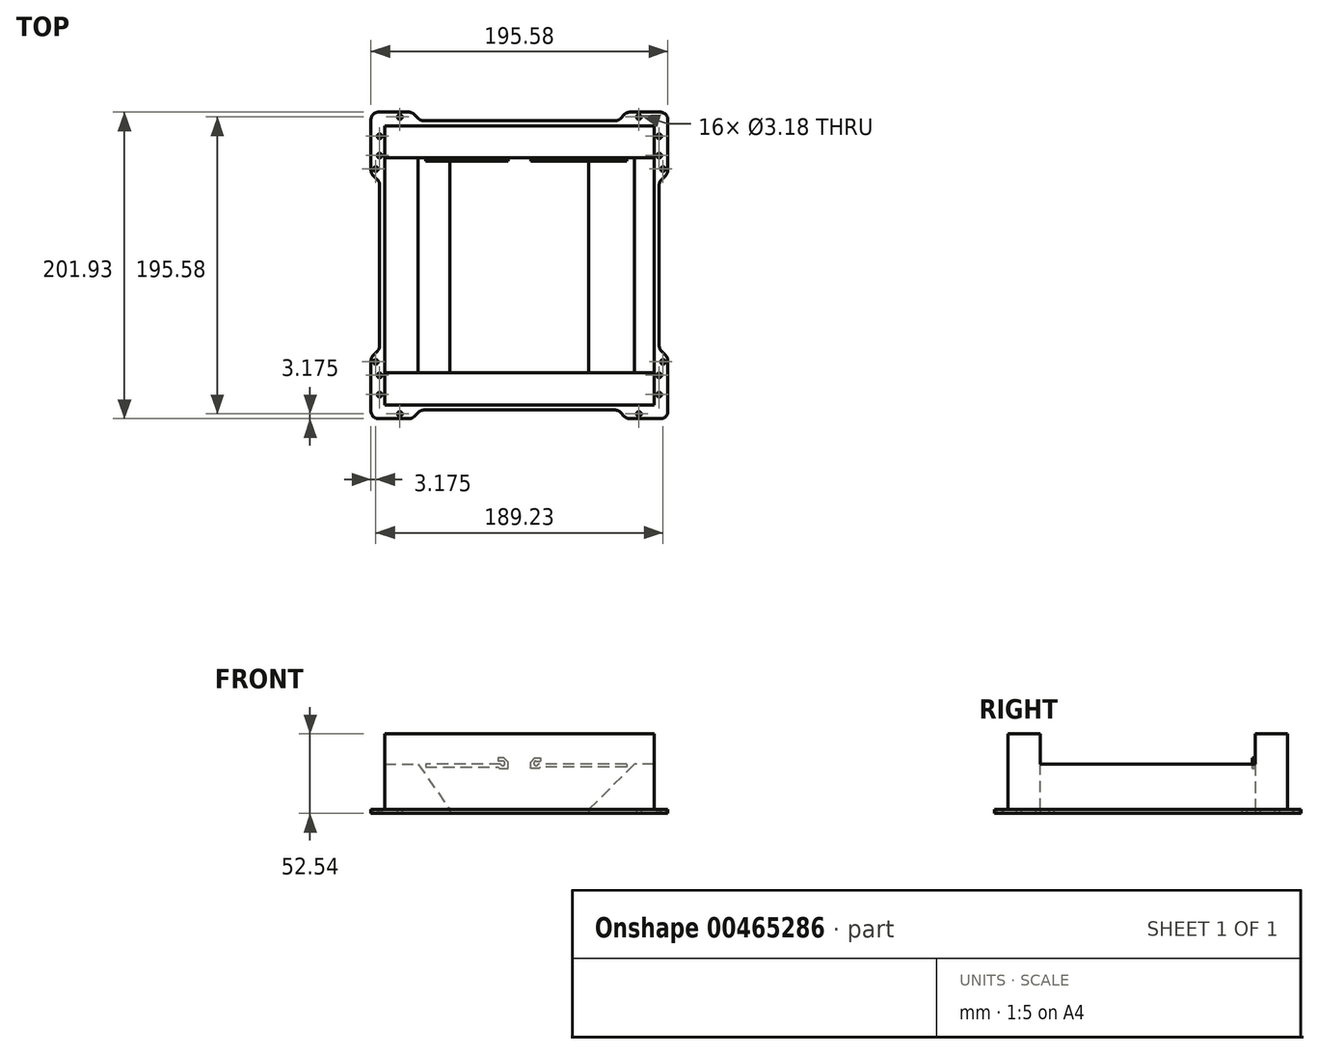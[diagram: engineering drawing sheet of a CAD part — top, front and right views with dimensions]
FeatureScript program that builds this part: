
annotation { "Feature Type Name" : "Feature", "Feature Type Description" : "" }
export const myFeature = defineFeature(function(context is Context, id is Id, definition is map)
    precondition{}
    {
        {
            var Q0;
            Q0=qCreatedBy(makeId("Top.planeOp"),FACE);
            var sketch = newSketch(context, id + "F0", { "sketchPlane" : qUnion([Q0])});
            skLineSegment(sketch, "E0.bottom", {"start": v(5, 0) * mm, "end": v(25, 0) * mm});
            skLineSegment(sketch, "E0.top", {"start": v(5, 201.93) * mm, "end": v(25, 201.93) * mm});
            skLineSegment(sketch, "E0.left", {"start": v(0, 5) * mm, "end": v(0, 38.18) * mm});
            skLineSegment(sketch, "E0.right", {"start": v(195.58, 5) * mm, "end": v(195.58, 38.18) * mm});
            skLineSegment(sketch, "E1.bottom", {"start": v(52.07, 171.77) * mm, "end": v(143.5, 171.77) * mm});
            skLineSegment(sketch, "E1.top", {"start": v(52.07, 30.17) * mm, "end": v(143.5, 30.17) * mm});
            skLineSegment(sketch, "E1.left", {"start": v(52.07, 171.77) * mm, "end": v(52.07, 30.17) * mm});
            skLineSegment(sketch, "E1.right", {"start": v(143.5, 171.77) * mm, "end": v(143.5, 30.17) * mm});
            skLineSegment(sketch, "E2", {"start": v(97.79, 232) * mm, "end": v(97.79, -11.17) * mm, "construction": true});
            skPoint(sketch, "E2.startSnap0", {"position": v(97.79, 201.93) * mm});
            skLineSegment(sketch, "E3", {"start": v(-12.15, 100.97) * mm, "end": v(206.64, 100.97) * mm, "construction": true});
            skPoint(sketch, "E3.startSnap0", {"position": v(0, 100.97) * mm});
            skPoint(sketch, "E4.visualSharp", {"position": v(0, 201.93) * mm});
            skArc(sketch, "E4.filletArc", {"start": v(5, 201.93) * mm, "mid": v(1.46, 200.47) * mm, "end": v(0, 196.93) * mm});
            skPoint(sketch, "E5.visualSharp", {"position": v(195.58, 201.93) * mm});
            skArc(sketch, "E5.filletArc", {"start": v(195.58, 196.93) * mm, "mid": v(194.12, 200.47) * mm, "end": v(190.58, 201.93) * mm});
            skArc(sketch, "E6.filletArc", {"start": v(0, 5) * mm, "mid": v(1.46, 1.46) * mm, "end": v(5, 0) * mm});
            skPoint(sketch, "E7.visualSharp", {"position": v(195.58, 0) * mm});
            skArc(sketch, "E7.filletArc", {"start": v(190.58, 0) * mm, "mid": v(194.12, 1.46) * mm, "end": v(195.58, 5) * mm});
            skLineSegment(sketch, "E8.bottom", {"start": v(34.86, 196.21) * mm, "end": v(160.72, 196.22) * mm});
            skLineSegment(sketch, "E8.top", {"start": v(34.86, 5.71) * mm, "end": v(160.72, 5.72) * mm});
            skLineSegment(sketch, "E8.left", {"start": v(5.72, 153.9) * mm, "end": v(5.72, 48.04) * mm});
            skLineSegment(sketch, "E8.right", {"start": v(189.87, 153.9) * mm, "end": v(189.87, 48.04) * mm});
            skLineSegment(sketch, "E9", {"start": v(1.46, 160.22) * mm, "end": v(4.25, 157.43) * mm});
            skLineSegment(sketch, "E10.trimOffspring", {"start": v(0, 163.75) * mm, "end": v(0, 196.93) * mm});
            skLineSegment(sketch, "E11.MirrorCS", {"start": v(194.12, 160.22) * mm, "end": v(191.33, 157.43) * mm});
            skLineSegment(sketch, "E12.MirrorCS", {"start": v(1.46, 41.71) * mm, "end": v(4.25, 44.5) * mm});
            skLineSegment(sketch, "E13.MirrorCS", {"start": v(194.12, 41.71) * mm, "end": v(191.33, 44.5) * mm});
            skLineSegment(sketch, "E14.trimOffspring", {"start": v(195.58, 163.75) * mm, "end": v(195.58, 196.93) * mm});
            skLineSegment(sketch, "E15", {"start": v(28.54, 200.47) * mm, "end": v(31.33, 197.68) * mm});
            skLineSegment(sketch, "E16.MirrorCS", {"start": v(167.04, 200.47) * mm, "end": v(164.25, 197.68) * mm});
            skLineSegment(sketch, "E17.MirrorCS", {"start": v(167.04, 1.46) * mm, "end": v(164.25, 4.25) * mm});
            skLineSegment(sketch, "E18.MirrorCS", {"start": v(28.54, 1.46) * mm, "end": v(31.33, 4.25) * mm});
            skLineSegment(sketch, "E19.trimOffspring", {"start": v(170.58, 201.93) * mm, "end": v(190.58, 201.93) * mm});
            skLineSegment(sketch, "E20.trimOffspring", {"start": v(170.58, 0) * mm, "end": v(190.58, 0) * mm});
            skPoint(sketch, "E21.visualSharp", {"position": v(0, 161.68) * mm});
            skArc(sketch, "E21.filletArc", {"start": v(0, 163.75) * mm, "mid": v(0.38, 161.84) * mm, "end": v(1.46, 160.22) * mm});
            skPoint(sketch, "E22.visualSharp", {"position": v(5.71, 155.97) * mm});
            skArc(sketch, "E22.filletArc", {"start": v(5.72, 153.9) * mm, "mid": v(5.33, 155.8) * mm, "end": v(4.25, 157.43) * mm});
            skPoint(sketch, "E23.visualSharp", {"position": v(27.08, 201.93) * mm});
            skArc(sketch, "E23.filletArc", {"start": v(28.54, 200.47) * mm, "mid": v(26.92, 201.55) * mm, "end": v(25, 201.93) * mm});
            skPoint(sketch, "E24.visualSharp", {"position": v(32.79, 196.21) * mm});
            skArc(sketch, "E24.filletArc", {"start": v(31.33, 197.68) * mm, "mid": v(32.95, 196.6) * mm, "end": v(34.86, 196.21) * mm});
            skPoint(sketch, "E25.visualSharp", {"position": v(162.79, 196.21) * mm});
            skArc(sketch, "E25.filletArc", {"start": v(160.72, 196.21) * mm, "mid": v(162.63, 196.6) * mm, "end": v(164.25, 197.68) * mm});
            skPoint(sketch, "E26.visualSharp", {"position": v(168.5, 201.93) * mm});
            skArc(sketch, "E26.filletArc", {"start": v(170.58, 201.93) * mm, "mid": v(168.66, 201.55) * mm, "end": v(167.04, 200.47) * mm});
            skPoint(sketch, "E27.visualSharp", {"position": v(195.58, 161.68) * mm});
            skArc(sketch, "E27.filletArc", {"start": v(194.12, 160.22) * mm, "mid": v(195.2, 161.84) * mm, "end": v(195.58, 163.75) * mm});
            skPoint(sketch, "E28.visualSharp", {"position": v(189.86, 155.97) * mm});
            skArc(sketch, "E28.filletArc", {"start": v(191.33, 157.43) * mm, "mid": v(190.25, 155.8) * mm, "end": v(189.86, 153.9) * mm});
            skPoint(sketch, "E29.visualSharp", {"position": v(189.86, 45.97) * mm});
            skArc(sketch, "E29.filletArc", {"start": v(189.86, 48.04) * mm, "mid": v(190.25, 46.12) * mm, "end": v(191.33, 44.5) * mm});
            skPoint(sketch, "E30.visualSharp", {"position": v(195.58, 40.25) * mm});
            skArc(sketch, "E30.filletArc", {"start": v(195.58, 38.18) * mm, "mid": v(195.2, 40.1) * mm, "end": v(194.12, 41.71) * mm});
            skPoint(sketch, "E31.visualSharp", {"position": v(162.79, 5.72) * mm});
            skArc(sketch, "E31.filletArc", {"start": v(164.25, 4.25) * mm, "mid": v(162.63, 5.33) * mm, "end": v(160.72, 5.72) * mm});
            skPoint(sketch, "E32.visualSharp", {"position": v(168.5, 0) * mm});
            skArc(sketch, "E32.filletArc", {"start": v(167.04, 1.46) * mm, "mid": v(168.66, 0.38) * mm, "end": v(170.58, 0) * mm});
            skPoint(sketch, "E33.visualSharp", {"position": v(32.79, 5.72) * mm});
            skArc(sketch, "E33.filletArc", {"start": v(34.86, 5.72) * mm, "mid": v(32.95, 5.33) * mm, "end": v(31.33, 4.25) * mm});
            skPoint(sketch, "E34.visualSharp", {"position": v(27.08, 0) * mm});
            skArc(sketch, "E34.filletArc", {"start": v(25, 0) * mm, "mid": v(26.92, 0.38) * mm, "end": v(28.54, 1.46) * mm});
            skPoint(sketch, "E35.visualSharp", {"position": v(5.71, 45.97) * mm});
            skArc(sketch, "E35.filletArc", {"start": v(4.25, 44.5) * mm, "mid": v(5.33, 46.12) * mm, "end": v(5.72, 48.04) * mm});
            skPoint(sketch, "E36.visualSharp", {"position": v(0, 40.25) * mm});
            skArc(sketch, "E36.filletArc", {"start": v(1.46, 41.71) * mm, "mid": v(0.38, 40.1) * mm, "end": v(0, 38.18) * mm});
            skCircle(sketch, "E37", {"center": v(3.17, 164.46) * mm, "radius": 1.59 * mm});
            skCircle(sketch, "E38", {"center": v(5.71, 173.35) * mm, "radius": 1.59 * mm});
            skCircle(sketch, "E39", {"center": v(5.71, 186.05) * mm, "radius": 1.59 * mm});
            skCircle(sketch, "E40", {"center": v(19.05, 198.76) * mm, "radius": 1.59 * mm});
            skCircle(sketch, "E41.MirrorC", {"center": v(3.17, 37.47) * mm, "radius": 1.59 * mm});
            skCircle(sketch, "E42.MirrorC", {"center": v(5.71, 28.58) * mm, "radius": 1.59 * mm});
            skCircle(sketch, "E43.MirrorC", {"center": v(5.71, 15.88) * mm, "radius": 1.59 * mm});
            skCircle(sketch, "E44.MirrorC", {"center": v(19.05, 3.17) * mm, "radius": 1.59 * mm});
            skCircle(sketch, "E45.MirrorC", {"center": v(176.53, 198.76) * mm, "radius": 1.59 * mm});
            skCircle(sketch, "E46.MirrorC", {"center": v(189.86, 186.05) * mm, "radius": 1.59 * mm});
            skCircle(sketch, "E47.MirrorC", {"center": v(189.87, 173.35) * mm, "radius": 1.59 * mm});
            skCircle(sketch, "E48.MirrorC", {"center": v(192.4, 164.46) * mm, "radius": 1.59 * mm});
            skCircle(sketch, "E49.MirrorC", {"center": v(192.4, 37.47) * mm, "radius": 1.59 * mm});
            skCircle(sketch, "E50.MirrorC", {"center": v(189.87, 28.58) * mm, "radius": 1.59 * mm});
            skCircle(sketch, "E51.MirrorC", {"center": v(189.86, 15.88) * mm, "radius": 1.59 * mm});
            skCircle(sketch, "E52.MirrorC", {"center": v(176.53, 3.17) * mm, "radius": 1.59 * mm});
            skSolve(sketch);
        }
        {
            var Q0;
            Q0 = qSketchRegion(id + "F0", true);
            extrude(context, id + "F1", {"entities" : qUnion([Q0]), "depth" : 2.54 * mm});
        }
        {
            var Q0;
            Q0=makeQuery(id+"F1.opExtrude","CAP_FACE",FACE,{"disambiguationData":[OSD([sQuery(id+"F0.wireOp",EDGE,"E0.bottom"),sQuery(id+"F0.wireOp",EDGE,"E0.top"),sQuery(id+"F0.wireOp",EDGE,"E0.left"),sQuery(id+"F0.wireOp",EDGE,"E0.right"),sQuery(id+"F0.wireOp",EDGE,"E1.bottom"),sQuery(id+"F0.wireOp",EDGE,"E1.top"),sQuery(id+"F0.wireOp",EDGE,"E1.left"),sQuery(id+"F0.wireOp",EDGE,"E1.right"),sQuery(id+"F0.wireOp",EDGE,"E4.filletArc"),sQuery(id+"F0.wireOp",EDGE,"E5.filletArc"),sQuery(id+"F0.wireOp",EDGE,"E6.filletArc"),sQuery(id+"F0.wireOp",EDGE,"E7.filletArc"),sQuery(id+"F0.wireOp",EDGE,"E8.bottom"),sQuery(id+"F0.wireOp",EDGE,"E8.top"),sQuery(id+"F0.wireOp",EDGE,"E8.left"),sQuery(id+"F0.wireOp",EDGE,"E8.right"),sQuery(id+"F0.wireOp",EDGE,"E9"),sQuery(id+"F0.wireOp",EDGE,"E10.trimOffspring"),sQuery(id+"F0.wireOp",EDGE,"E11.MirrorCS"),sQuery(id+"F0.wireOp",EDGE,"E12.MirrorCS"),sQuery(id+"F0.wireOp",EDGE,"E13.MirrorCS"),sQuery(id+"F0.wireOp",EDGE,"E14.trimOffspring"),sQuery(id+"F0.wireOp",EDGE,"E15"),sQuery(id+"F0.wireOp",EDGE,"E16.MirrorCS"),sQuery(id+"F0.wireOp",EDGE,"E17.MirrorCS"),sQuery(id+"F0.wireOp",EDGE,"E18.MirrorCS"),sQuery(id+"F0.wireOp",EDGE,"E19.trimOffspring"),sQuery(id+"F0.wireOp",EDGE,"E20.trimOffspring"),sQuery(id+"F0.wireOp",EDGE,"E21.filletArc"),sQuery(id+"F0.wireOp",EDGE,"E22.filletArc"),sQuery(id+"F0.wireOp",EDGE,"E23.filletArc"),sQuery(id+"F0.wireOp",EDGE,"E24.filletArc"),sQuery(id+"F0.wireOp",EDGE,"E25.filletArc"),sQuery(id+"F0.wireOp",EDGE,"E26.filletArc"),sQuery(id+"F0.wireOp",EDGE,"E27.filletArc"),sQuery(id+"F0.wireOp",EDGE,"E28.filletArc"),sQuery(id+"F0.wireOp",EDGE,"E29.filletArc"),sQuery(id+"F0.wireOp",EDGE,"E30.filletArc"),sQuery(id+"F0.wireOp",EDGE,"E31.filletArc"),sQuery(id+"F0.wireOp",EDGE,"E32.filletArc"),sQuery(id+"F0.wireOp",EDGE,"E33.filletArc"),sQuery(id+"F0.wireOp",EDGE,"E34.filletArc"),sQuery(id+"F0.wireOp",EDGE,"E35.filletArc"),sQuery(id+"F0.wireOp",EDGE,"E36.filletArc"),sQuery(id+"F0.wireOp",EDGE,"E37"),sQuery(id+"F0.wireOp",EDGE,"E38"),sQuery(id+"F0.wireOp",EDGE,"E39"),sQuery(id+"F0.wireOp",EDGE,"E40"),sQuery(id+"F0.wireOp",EDGE,"E41.MirrorC"),sQuery(id+"F0.wireOp",EDGE,"E42.MirrorC"),sQuery(id+"F0.wireOp",EDGE,"E43.MirrorC"),sQuery(id+"F0.wireOp",EDGE,"E44.MirrorC"),sQuery(id+"F0.wireOp",EDGE,"E45.MirrorC"),sQuery(id+"F0.wireOp",EDGE,"E46.MirrorC"),sQuery(id+"F0.wireOp",EDGE,"E47.MirrorC"),sQuery(id+"F0.wireOp",EDGE,"E48.MirrorC"),sQuery(id+"F0.wireOp",EDGE,"E49.MirrorC"),sQuery(id+"F0.wireOp",EDGE,"E50.MirrorC"),sQuery(id+"F0.wireOp",EDGE,"E51.MirrorC"),sQuery(id+"F0.wireOp",EDGE,"E52.MirrorC")])],"isStart":false});
            var sketch = newSketch(context, id + "F2", { "sketchPlane" : qUnion([Q0])});
            skLineSegment(sketch, "E53.bottom", {"start": v(9, 171.77) * mm, "end": v(186.58, 171.77) * mm});
            skLineSegment(sketch, "E53.top", {"start": v(9, 192.93) * mm, "end": v(186.58, 192.93) * mm});
            skLineSegment(sketch, "E53.left", {"start": v(9, 171.77) * mm, "end": v(9, 192.93) * mm});
            skLineSegment(sketch, "E53.right", {"start": v(186.58, 171.77) * mm, "end": v(186.58, 192.93) * mm});
            skLineSegment(sketch, "E54.bottom", {"start": v(9, 30.17) * mm, "end": v(186.58, 30.17) * mm});
            skLineSegment(sketch, "E54.top", {"start": v(9, 9) * mm, "end": v(186.58, 9) * mm});
            skLineSegment(sketch, "E54.left", {"start": v(9, 30.17) * mm, "end": v(9, 9) * mm});
            skLineSegment(sketch, "E54.right", {"start": v(186.58, 30.17) * mm, "end": v(186.58, 9) * mm});
            skSolve(sketch);
        }
        {
            var Q0;
            Q0=makeQuery(id+"F2.imprint","IMPRINT",FACE,{"disambiguationData":[TD([[makeQuery(id+"F2.imprint","IMPRINT",EDGE,{"derivedFrom":sQuery(id+"F2.wireOp",EDGE,"E53.top")}),-1.0]])]});
            var Q1;
            Q1=makeQuery(id+"F2.imprint","IMPRINT",FACE,{"disambiguationData":[TD([[makeQuery(id+"F2.imprint","IMPRINT",EDGE,{"derivedFrom":sQuery(id+"F2.wireOp",EDGE,"E54.top")}),1.0]])]});
            extrude(context, id + "F3", {"entities" : qUnion([Q0, Q1]), "operationType" : NewBodyOperationType.ADD, "depth" : 50 * mm});
        }
        {
            var Q0;
            Q0=makeQuery(id+"F3.boolean.opBoolean","MERGE",FACE,{"derivedFrom":[makeQuery(id+"F1.opExtrude","SWEPT_FACE",FACE,{"disambiguationData":[OSD([sQuery(id+"F0.wireOp",EDGE,"E1.bottom")])]}),makeQuery(id+"F3.opExtrude","SWEPT_FACE",FACE,{"disambiguationData":[OSD([sQuery(id+"F2.wireOp",EDGE,"E53.bottom")])]})]});
            var sketch = newSketch(context, id + "F4", { "sketchPlane" : qUnion([Q0])});
            skLineSegment(sketch, "E55", {"start": v(52.07, 2.54) * mm, "end": v(9, 2.54) * mm});
            skLineSegment(sketch, "E56", {"start": v(9, 2.54) * mm, "end": v(9, 32.54) * mm});
            skLineSegment(sketch, "E57", {"start": v(9, 32.54) * mm, "end": v(31.06, 32.54) * mm});
            skLineSegment(sketch, "E58", {"start": v(31.06, 32.54) * mm, "end": v(52.07, 2.54) * mm});
            skLineSegment(sketch, "E59", {"start": v(186.58, 2.54) * mm, "end": v(186.58, 32.54) * mm});
            skLineSegment(sketch, "E60", {"start": v(186.58, 32.54) * mm, "end": v(173.5, 32.54) * mm});
            skLineSegment(sketch, "E61", {"start": v(173.5, 32.54) * mm, "end": v(143.51, 2.54) * mm});
            skLineSegment(sketch, "E62", {"start": v(143.5, 2.54) * mm, "end": v(186.58, 2.54) * mm});
            skSolve(sketch);
        }
        {
            var Q0;
            Q0 = qSketchRegion(id + "F4", true);
            var Q1;
            Q1=makeQuery(id+"F4.imprint","IMPRINT",FACE,{"disambiguationData":[TD([[makeQuery(id+"F4.imprint","IMPRINT",EDGE,{"derivedFrom":sQuery(id+"F4.wireOp",EDGE,"E55")}),1.0]])]});
            extrude(context, id + "F5", {"entities" : qUnion([Q0, Q1]), "operationType" : NewBodyOperationType.ADD, "endBound" : BoundingType.UP_TO_NEXT, "depth" : 25 * mm});
        }
        {
            var Q0;
            Q0=makeQuery(id+"F3.boolean.opBoolean","MERGE",FACE,{"derivedFrom":[makeQuery(id+"F1.opExtrude","SWEPT_FACE",FACE,{"disambiguationData":[OSD([sQuery(id+"F0.wireOp",EDGE,"E1.bottom")])]}),makeQuery(id+"F3.opExtrude","SWEPT_FACE",FACE,{"disambiguationData":[OSD([sQuery(id+"F2.wireOp",EDGE,"E53.bottom")])]})]});
            var sketch = newSketch(context, id + "F6", { "sketchPlane" : qUnion([Q0])});
            skLineSegment(sketch, "E63", {"start": v(83.8, 30.54) * mm, "end": v(84.8, 29.54) * mm});
            skLineSegment(sketch, "E64", {"start": v(84.8, 29.54) * mm, "end": v(90.3, 29.54) * mm});
            skLineSegment(sketch, "E65", {"start": v(90.3, 29.54) * mm, "end": v(90.3, 33.93) * mm});
            skLineSegment(sketch, "E66", {"start": v(90.3, 33.93) * mm, "end": v(87.68, 36.54) * mm});
            skLineSegment(sketch, "E67", {"start": v(87.68, 36.54) * mm, "end": v(83.8, 36.54) * mm});
            skLineSegment(sketch, "E68", {"start": v(83.8, 36.54) * mm, "end": v(83.8, 34.54) * mm});
            skArc(sketch, "E69", {"start": v(86.8, 34.54) * mm, "mid": v(88.01, 32.17) * mm, "end": v(85.38, 32.54) * mm});
            skLineSegment(sketch, "E70", {"start": v(86.8, 34.54) * mm, "end": v(83.8, 34.54) * mm});
            skPoint(sketch, "E71.bottom.end.orphan", {"position": v(83.8, 33.74) * mm});
            skLineSegment(sketch, "E72", {"start": v(97.8, 0) * mm, "end": v(97.8, 46.53) * mm, "construction": true});
            skLineSegment(sketch, "E73.MirrorCS", {"start": v(105.29, 29.54) * mm, "end": v(105.29, 33.93) * mm});
            skLineSegment(sketch, "E74.MirrorCS", {"start": v(105.29, 33.93) * mm, "end": v(107.9, 36.54) * mm});
            skLineSegment(sketch, "E75.MirrorCS", {"start": v(107.9, 36.54) * mm, "end": v(111.8, 36.54) * mm});
            skLineSegment(sketch, "E76.MirrorCS", {"start": v(111.8, 36.54) * mm, "end": v(111.8, 34.54) * mm});
            skLineSegment(sketch, "E77.MirrorCS", {"start": v(108.79, 34.54) * mm, "end": v(111.8, 34.54) * mm});
            skArc(sketch, "E78.MirrorCS", {"start": v(108.79, 34.54) * mm, "mid": v(107.57, 32.17) * mm, "end": v(110.2, 32.54) * mm});
            skLineSegment(sketch, "E79.MirrorCS", {"start": v(110.8, 29.54) * mm, "end": v(105.29, 29.54) * mm});
            skLineSegment(sketch, "E80.MirrorCS", {"start": v(111.8, 30.54) * mm, "end": v(110.8, 29.54) * mm});
            skLineSegment(sketch, "E81.MirrorCS", {"start": v(168.5, 30.54) * mm, "end": v(111.8, 30.54) * mm});
            skLineSegment(sketch, "E82.MirrorCS", {"start": v(168.5, 32.54) * mm, "end": v(110.2, 32.54) * mm});
            skLineSegment(sketch, "E83.MirrorCS", {"start": v(168.5, 32.54) * mm, "end": v(168.5, 30.54) * mm});
            skLineSegment(sketch, "E84", {"start": v(85.38, 32.54) * mm, "end": v(36.06, 32.54) * mm});
            skLineSegment(sketch, "E85", {"start": v(36.06, 30.54) * mm, "end": v(83.8, 30.54) * mm});
            skLineSegment(sketch, "E86", {"start": v(36.06, 32.54) * mm, "end": v(36.06, 30.54) * mm});
            skSolve(sketch);
        }
        {
            var Q0;
            Q0=makeQuery(id+"F6.imprint","IMPRINT",FACE,{"disambiguationData":[TD([[makeQuery(id+"F6.imprint","IMPRINT",EDGE,{"derivedFrom":sQuery(id+"F6.wireOp",EDGE,"E71.top")}),-1.0]])]});
            var Q1;
            Q1=makeQuery(id+"F6.imprint","IMPRINT",FACE,{"disambiguationData":[TD([[makeQuery(id+"F6.imprint","IMPRINT",EDGE,{"derivedFrom":sQuery(id+"F6.wireOp",EDGE,"E73.MirrorCS")}),-1.0]])]});
            var Q2;
            Q2=makeQuery(id+"F6.imprint","IMPRINT",FACE,{"disambiguationData":[TD([[makeQuery(id+"F6.imprint","IMPRINT",EDGE,{"derivedFrom":sQuery(id+"F6.wireOp",EDGE,"E63")}),1.0]])]});
            extrude(context, id + "F7", {"entities" : qUnion([Q0, Q1, Q2]), "operationType" : NewBodyOperationType.ADD, "depth" : 2 * mm});
        }
    });
